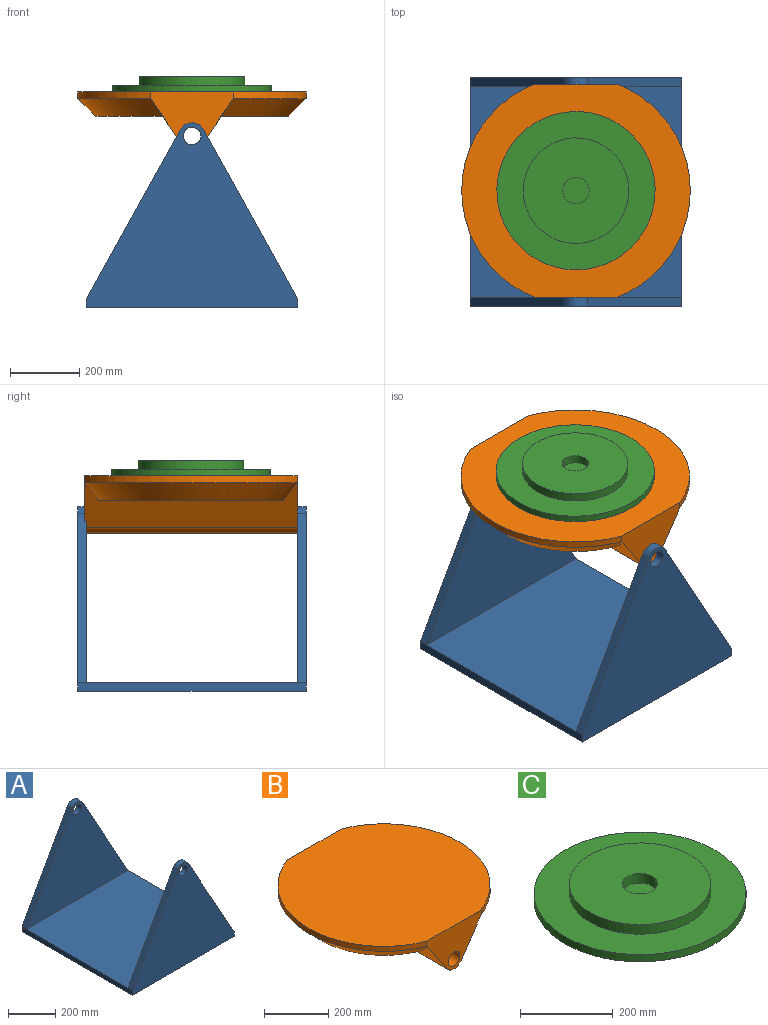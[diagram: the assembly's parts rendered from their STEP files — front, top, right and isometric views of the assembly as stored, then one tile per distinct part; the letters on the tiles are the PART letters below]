
ASSEMBLY  parts=3 mates=2
PART A: 16 faces, bbox 609.6x660.4x533.4 mm
  f0: plane 660.4x25.4mm, normal (-1,0,0), area 16774.2mm2, adj f2,f3,f6,f8,f13,f15
  f1: plane 660.4x25.4mm, normal (1,0,0), area 16774.2mm2, adj f2,f3,f4,f8,f11,f15
  f2: plane 609.6x609.6mm, normal (0,0,1), area 371612.2mm2, adj f0,f1,f9,f10
  f3: plane 660.4x609.6mm, normal (0,0,-1), area 402579.8mm2, adj f0,f1,f8,f15
  f4: plane 488.41x271.5mm, normal (0.87,0,0.49), area 14193.5mm2, adj f1,f5,f8,f9
  f5: cylinder r=38.1mm len=66.6mm, axis (0,1,0), area 2058.3mm2, adj f4,f6,f8,f9
  f6: plane 488.41x271.5mm, normal (-0.87,0,0.49), area 14193.5mm2, adj f0,f5,f8,f9
  f7: cylinder r=25.4mm len=50.8mm, axis (0,1,0), area 4053.7mm2, adj f8,f9
  f8: plane 609.6x533.4mm, normal (0,-1,0), area 179516.5mm2, adj f0,f1,f3,f4,f5,f6,f7
  f9: plane 609.6x508mm, normal (0,1,0), area 164032.7mm2, adj f2,f4,f5,f6,f7
  f10: plane 609.6x508mm, normal (0,-1,0), area 164032.7mm2, adj f2,f11,f12,f13,f14
  f11: plane 488.41x271.5mm, normal (0.87,0,0.49), area 14193.5mm2, adj f1,f10,f12,f15
  f12: cylinder r=38.1mm len=66.6mm, axis (0,-1,0), area 2058.3mm2, adj f10,f11,f13,f15
  f13: plane 488.41x271.5mm, normal (-0.87,0,0.49), area 14193.5mm2, adj f0,f10,f12,f15
  f14: cylinder r=25.4mm len=50.8mm, axis (0,-1,0), area 4053.7mm2, adj f10,f15
  f15: plane 609.6x533.4mm, normal (0,1,0), area 179516.5mm2, adj f0,f1,f3,f11,f12,f13,f14
PART B: 13 faces, bbox 660.4x629.3x165.1 mm
  f0: cone r=330.2mm half-angle=45deg, axis (0,0,1), area 53862mm2, adj f1,f2,f10
  f1: plane 532.5x194.7mm, normal (0,0,-1), area 76027.1mm2, adj f0,f10
  f2: cylinder r=330.2mm len=615.95mm, axis (0,0,1), area 15119.5mm2, adj f0,f4,f7,f8
  f3: cylinder r=330.2mm len=615.95mm, axis (0,0,1), area 15119.5mm2, adj f4,f5,f7,f8
  f4: plane 660.4x615.95mm, normal (0,0,1), area 335427mm2, adj f2,f3,f7,f8
  f5: cone r=330.2mm half-angle=45deg, axis (0,0,1), area 53862mm2, adj f3,f6,f12
  f6: plane 532.5x194.7mm, normal (0,0,-1), area 76027.1mm2, adj f5,f12
  f7: plane 238.19x165.1mm, normal (0,-1,0), area 22732.8mm2, adj f2,f3,f4,f9,f10,f11,f12
  f8: plane 238.19x165.1mm, normal (0,1,0), area 22732.8mm2, adj f2,f3,f4,f9,f10,f11,f12
  f9: cylinder r=38.1mm len=615.95mm, axis (0,-1,0), area 45793.1mm2, adj f7,f8,f10,f12
  f10: plane 615.96x129.32mm, normal (0.83,0,-0.56), area 60945.5mm2, adj f0,f1,f7,f8,f9
  f11: cylinder r=25.4mm len=615.95mm, axis (0,-1,0), area 98301.3mm2, adj f7,f8
  f12: plane 615.96x129.32mm, normal (-0.83,0,-0.56), area 60945.5mm2, adj f5,f6,f7,f8,f9
PART C: 7 faces, bbox 457.2x457.2x44.5 mm
  f0: cylinder r=228.6mm len=457.2mm, axis (0,0,-1), area 27362.2mm2, adj f1,f2
  f1: plane 457.2x457.2mm, normal (0,0,1), area 91207.3mm2, adj f0,f4
  f2: plane 457.2x457.2mm, normal (0,0,-1), area 164173.2mm2, adj f0
  f3: cylinder r=38.1mm len=76.2mm, axis (0,0,-1), area 6080.5mm2, adj f5,f6
  f4: cylinder r=152.4mm len=304.8mm, axis (0,0,-1), area 24322mm2, adj f1,f5
  f5: plane 304.8x304.8mm, normal (0,0,1), area 68405.5mm2, adj f3,f4
  f6: plane 76.2x76.2mm, normal (0,0,1), area 4560.4mm2, adj f3
PLACE A t=(-1.08,-3.58,-193.7)mm fixed
PLACE B t=(-1.08,-0.41,-193.7)mm
PLACE C rot(axis=(0,0,1),114.3deg) t=(-1.08,-0.41,-193.7)mm
MATE revolute B.f0 <-> C.f0  axis (0,0,1) through (-1.08,-0.41,428.6)mm
MATE revolute B.f9 <-> A.f5  axis (0,-1,0) through (-1.08,-308.38,301.6)mm
